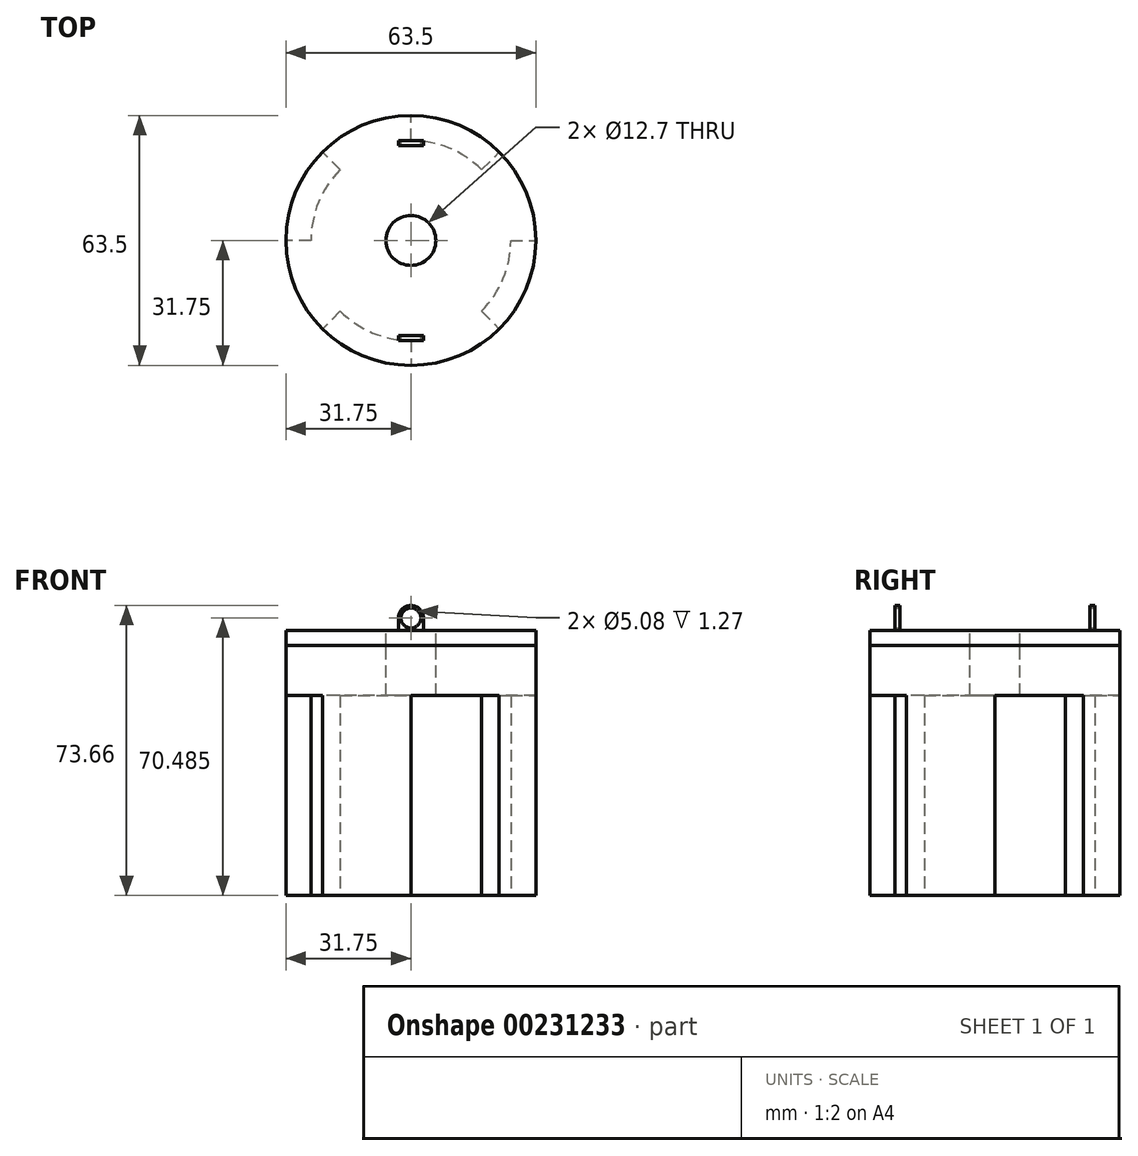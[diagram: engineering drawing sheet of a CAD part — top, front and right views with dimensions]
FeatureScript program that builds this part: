
annotation { "Feature Type Name" : "Feature", "Feature Type Description" : "" }
export const myFeature = defineFeature(function(context is Context, id is Id, definition is map)
    precondition{}
    {
        {
            var Q0;
            Q0=qCreatedBy(makeId("Top.planeOp"),FACE);
            var sketch = newSketch(context, id + "F0", { "sketchPlane" : qUnion([Q0])});
            skCircle(sketch, "E0", {"center": v(0, 0) * mm, "radius": 31.75 * mm});
            skSolve(sketch);
        }
        {
            var Q0;
            Q0=makeQuery(id+"F0.imprint","IMPRINT",FACE,{"disambiguationData":[TD([[makeQuery(id+"F0.imprint","IMPRINT",EDGE,{"derivedFrom":sQuery(id+"F0.wireOp",EDGE,"E0")}),1.0]])]});
            extrude(context, id + "F1", {"entities" : qUnion([Q0]), "depth" : 63.5 * mm});
        }
        {
            var Q0;
            Q0=qCreatedBy(makeId("Top.planeOp"),FACE);
            var sketch = newSketch(context, id + "F2", { "sketchPlane" : qUnion([Q0])});
            skCircle(sketch, "E1", {"center": v(0, 0) * mm, "radius": 25.4 * mm});
            skSolve(sketch);
        }
        {
            var Q0;
            Q0=makeQuery(id+"F2.imprint","IMPRINT",FACE,{"disambiguationData":[TD([[makeQuery(id+"F2.imprint","IMPRINT",EDGE,{"derivedFrom":sQuery(id+"F2.wireOp",EDGE,"E1")}),1.0]])]});
            extrude(context, id + "F3", {"entities" : qUnion([Q0]), "operationType" : NewBodyOperationType.REMOVE, "depth" : 50.8 * mm});
        }
        {
            var Q0;
            Q0=qCreatedBy(makeId("Top.planeOp"),FACE);
            var sketch = newSketch(context, id + "F4", { "sketchPlane" : qUnion([Q0])});
            skLineSegment(sketch, "E2", {"start": v(25.4, 0) * mm, "end": v(35.24, 0) * mm});
            skLineSegment(sketch, "E3", {"start": v(0, 25.4) * mm, "end": v(0, 31.75) * mm});
            skLineSegment(sketch, "E4", {"start": v(17.96, 17.96) * mm, "end": v(22.45, 22.45) * mm});
            skLineSegment(sketch, "E5.MirrorCS", {"start": v(-17.96, 17.96) * mm, "end": v(-22.45, 22.45) * mm});
            skLineSegment(sketch, "E6.MirrorCS", {"start": v(-25.4, 0) * mm, "end": v(-35.24, 0) * mm});
            skLineSegment(sketch, "E7.MirrorCS", {"start": v(0, -25.4) * mm, "end": v(0, -31.75) * mm});
            skLineSegment(sketch, "E8.MirrorCS", {"start": v(17.96, -17.96) * mm, "end": v(22.45, -22.45) * mm});
            skLineSegment(sketch, "E9.MirrorCS", {"start": v(-17.96, -17.96) * mm, "end": v(-22.45, -22.45) * mm});
            skCircle(sketch, "E10.0", {"center": v(0, 0) * mm, "radius": 31.75 * mm});
            skPoint(sketch, "E11.orphan", {"position": v(-59.05, -59.05) * mm});
            skPoint(sketch, "E12.orphan", {"position": v(0, -40.51) * mm});
            skPoint(sketch, "E13.orphan", {"position": v(59.05, -59.05) * mm});
            skPoint(sketch, "E14.orphan", {"position": v(59.05, 59.05) * mm});
            skPoint(sketch, "E15.orphan", {"position": v(0, 40.51) * mm});
            skPoint(sketch, "E16.orphan", {"position": v(-59.05, 59.05) * mm});
            skPoint(sketch, "E17.orphan", {"position": v(-35.24, 0) * mm});
            skCircle(sketch, "E18.0", {"center": v(0, 0) * mm, "radius": 25.4 * mm});
            skSolve(sketch);
        }
        {
            var Q0;
            {var subQ5=sQuery(id+"F4.wireOp",EDGE,"E9.MirrorCS");Q0=makeQuery(id+"F4.imprint","IMPRINT",FACE,{"disambiguationData":[TD([[makeQuery(id+"F4.imprint","IMPRINT",EDGE,{"derivedFrom":subQ5}),-1.0]])]});}
            var Q1;
            {var subQ0=sQuery(id+"F4.wireOp",EDGE,"E7.MirrorCS");Q1=makeQuery(id+"F4.imprint","IMPRINT",FACE,{"disambiguationData":[TD([[makeQuery(id+"F4.imprint","IMPRINT",EDGE,{"derivedFrom":subQ0}),1.0]])]});}
            var Q2;
            {var subQ5=sQuery(id+"F4.wireOp",EDGE,"E4");Q2=makeQuery(id+"F4.imprint","IMPRINT",FACE,{"disambiguationData":[TD([[makeQuery(id+"F4.imprint","IMPRINT",EDGE,{"derivedFrom":subQ5}),-1.0]])]});}
            var Q3;
            {var subQ0=sQuery(id+"F4.wireOp",EDGE,"E3");Q3=makeQuery(id+"F4.imprint","IMPRINT",FACE,{"disambiguationData":[TD([[makeQuery(id+"F4.imprint","IMPRINT",EDGE,{"derivedFrom":subQ0}),1.0]])]});}
            extrude(context, id + "F5", {"entities" : qUnion([Q0, Q1, Q2, Q3]), "operationType" : NewBodyOperationType.REMOVE, "depth" : 50.8 * mm});
        }
        {
            var Q0;
            Q0=makeQuery(id+"F1.opExtrude","CAP_FACE",FACE,{"disambiguationData":[OSD([sQuery(id+"F0.wireOp",EDGE,"E0")])],"isStart":false});
            var sketch = newSketch(context, id + "F6", { "sketchPlane" : qUnion([Q0])});
            skCircle(sketch, "E19.0", {"center": v(0, 0) * mm, "radius": 31.75 * mm});
            skSolve(sketch);
        }
        {
            var Q0;
            Q0=makeQuery(id+"F6.imprint","IMPRINT",FACE,{"disambiguationData":[TD([[makeQuery(id+"F6.imprint","IMPRINT",EDGE,{"derivedFrom":sQuery(id+"F6.wireOp",EDGE,"E19.0")}),1.0]])]});
            extrude(context, id + "F7", {"entities" : qUnion([Q0]), "depth" : 3.8 * mm});
        }
        {
            var Q0;
            Q0=makeQuery(id+"F7.opExtrude","CAP_FACE",FACE,{"disambiguationData":[OSD([sQuery(id+"F6.wireOp",EDGE,"E19.0")])],"isStart":false});
            var sketch = newSketch(context, id + "F8", { "sketchPlane" : qUnion([Q0])});
            skCircle(sketch, "E20", {"center": v(0, 0) * mm, "radius": 6.35 * mm});
            skSolve(sketch);
        }
        {
            var Q0;
            Q0=makeQuery(id+"F8.imprint","IMPRINT",FACE,{"disambiguationData":[TD([[makeQuery(id+"F8.imprint","IMPRINT",EDGE,{"derivedFrom":sQuery(id+"F8.wireOp",EDGE,"E20")}),1.0]])]});
            extrude(context, id + "F9", {"entities" : qUnion([Q0]), "operationType" : NewBodyOperationType.REMOVE, "endBound" : BoundingType.THROUGH_ALL, "oppositeDirection" : true, "depth" : 127 * mm});
        }
        {
            var Q0;
            Q0=makeQuery(id+"F1.opExtrude","CAP_FACE",FACE,{"disambiguationData":[OSD([sQuery(id+"F0.wireOp",EDGE,"E0")])],"isStart":false});
            var sketch = newSketch(context, id + "F10", { "sketchPlane" : qUnion([Q0])});
            skCircle(sketch, "E21.0", {"center": v(0, 0) * mm, "radius": 6.35 * mm});
            skSolve(sketch);
        }
        {
            var Q0;
            Q0=makeQuery(id+"F10.imprint","IMPRINT",FACE,{"disambiguationData":[TD([[makeQuery(id+"F10.imprint","IMPRINT",EDGE,{"derivedFrom":sQuery(id+"F10.wireOp",EDGE,"E21.0")}),1.0]])]});
            extrude(context, id + "F11", {"entities" : qUnion([Q0]), "operationType" : NewBodyOperationType.REMOVE, "endBound" : BoundingType.THROUGH_ALL, "oppositeDirection" : true, "depth" : 25.4 * mm});
        }
        {
            var Q0;
            Q0=qCreatedBy(makeId("Front.planeOp"),FACE);
            var sketch = newSketch(context, id + "F12", { "sketchPlane" : qUnion([Q0])});
            skLineSegment(sketch, "E22.0", {"start": v(-31.75, 67.3) * mm, "end": v(31.75, 67.3) * mm});
            skPoint(sketch, "E23.endSnap0", {"position": v(0, 67.3) * mm});
            skPoint(sketch, "E24", {"position": v(0, 73.66) * mm});
            skPoint(sketch, "E25", {"position": v(0, 70.48) * mm});
            skArc(sketch, "E26", {"start": v(3.17, 70.48) * mm, "mid": v(0, 73.66) * mm, "end": v(-3.17, 70.48) * mm});
            skPoint(sketch, "E27", {"position": v(3.17, 70.48) * mm});
            skPoint(sketch, "E28.MirrorP", {"position": v(-3.17, 70.48) * mm});
            skLineSegment(sketch, "E29", {"start": v(-3.17, 70.48) * mm, "end": v(-3.17, 67.3) * mm});
            skLineSegment(sketch, "E30", {"start": v(3.17, 70.48) * mm, "end": v(3.17, 67.3) * mm});
            skCircle(sketch, "E31", {"center": v(0, 70.48) * mm, "radius": 2.54 * mm});
            skSolve(sketch);
        }
        {
            var Q0;
            Q0=makeQuery(id+"F12.imprint","IMPRINT",FACE,{"disambiguationData":[TD([[makeQuery(id+"F12.imprint","IMPRINT",EDGE,{"derivedFrom":sQuery(id+"F12.wireOp",EDGE,"E26")}),1.0]])]});
            extrude(context, id + "F13", {"entities" : qUnion([Q0]), "operationType" : NewBodyOperationType.ADD, "endBound" : BoundingType.SYMMETRIC, "depth" : 50.8 * mm});
        }
        {
            var Q0;
            Q0=makeQuery(id+"F12.imprint","IMPRINT",FACE,{"disambiguationData":[TD([[makeQuery(id+"F12.imprint","IMPRINT",EDGE,{"derivedFrom":sQuery(id+"F12.wireOp",EDGE,"E26")}),1.0]])]});
            extrude(context, id + "F14", {"entities" : qUnion([Q0]), "operationType" : NewBodyOperationType.REMOVE, "endBound" : BoundingType.SYMMETRIC, "depth" : 48.26 * mm});
        }
    });
